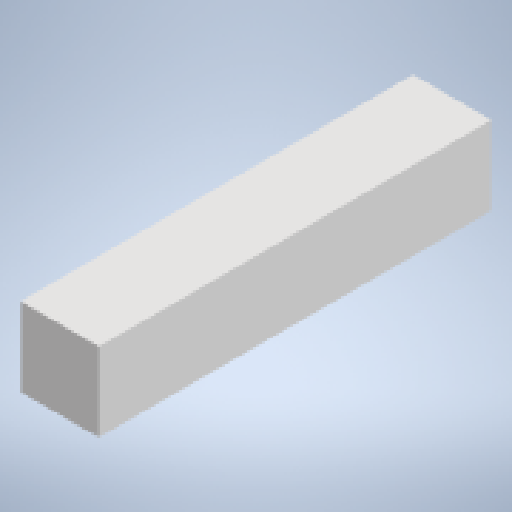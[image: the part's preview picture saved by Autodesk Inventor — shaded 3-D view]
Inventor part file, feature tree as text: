
AUTODESK INVENTOR PART (.ipt)
format: ipt  version: 2023 (Build 270158000, 158)  size: 135,680 bytes
history: native  units: mm
features: extrude x1, sketch x1
ambient origin geometry x8: Origin, YZ Plane, XZ Plane, XY Plane, X Axis, Y Axis, Z Axis, Center Point
bodies: Solid1 (feature_tree)
feature tree (2):
  extrude  "Extrusion1"  Depth=20.0mm
  sketch  "Sketch1"  dims[d0=20.0mm d1=20.0mm d2=100.0mm d3=0.0mm]
